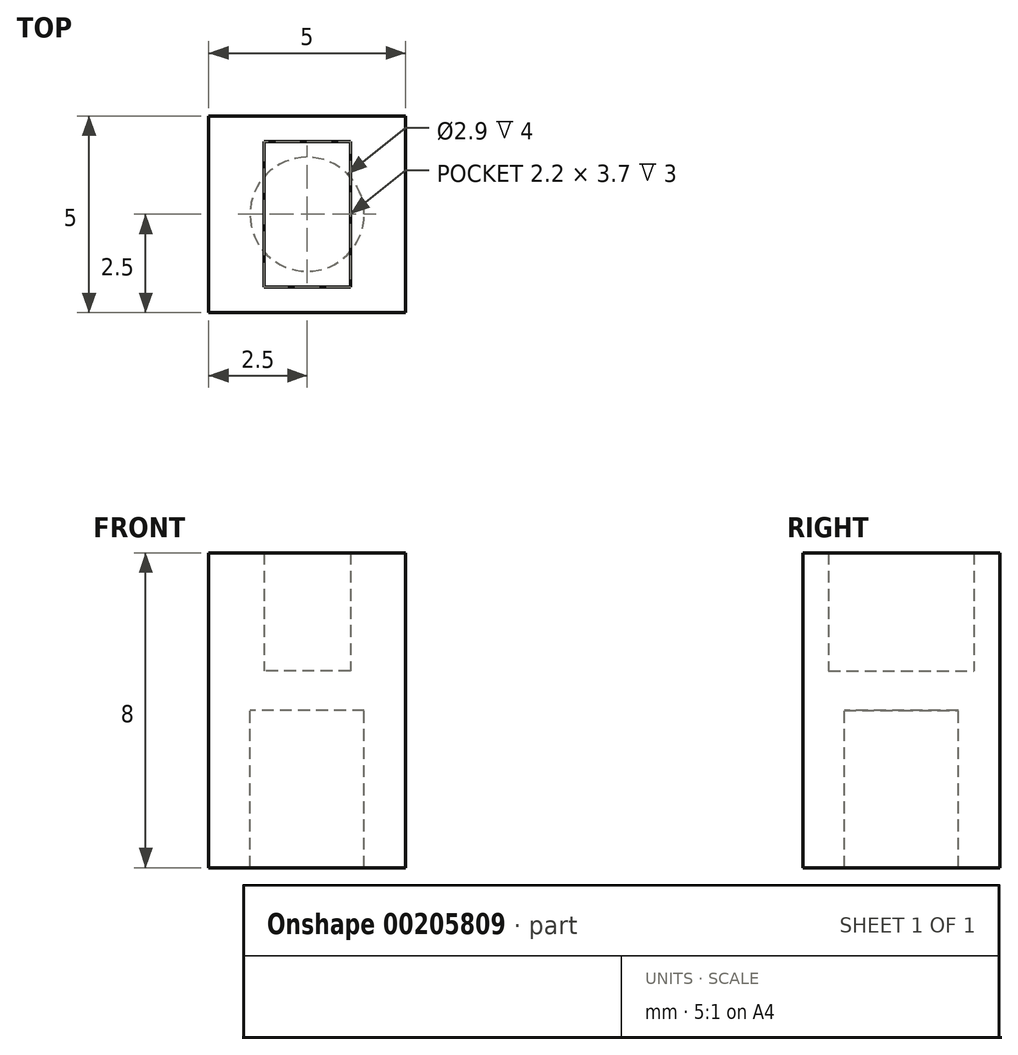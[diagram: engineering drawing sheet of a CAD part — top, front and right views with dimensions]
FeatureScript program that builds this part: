
annotation { "Feature Type Name" : "Feature", "Feature Type Description" : "" }
export const myFeature = defineFeature(function(context is Context, id is Id, definition is map)
    precondition{}
    {
        {
            var Q0;
            Q0=qCreatedBy(makeId("Top.planeOp"),FACE);
            var sketch = newSketch(context, id + "F0", { "sketchPlane" : qUnion([Q0])});
            skLineSegment(sketch, "E0.bottom", {"start": v(2.5, 2.5) * mm, "end": v(-2.5, 2.5) * mm});
            skLineSegment(sketch, "E0.top", {"start": v(2.5, -2.5) * mm, "end": v(-2.5, -2.5) * mm});
            skLineSegment(sketch, "E0.left", {"start": v(2.5, 2.5) * mm, "end": v(2.5, -2.5) * mm});
            skLineSegment(sketch, "E0.right", {"start": v(-2.5, 2.5) * mm, "end": v(-2.5, -2.5) * mm});
            skPoint(sketch, "E0.middle", {"position": v(0, 0) * mm});
            skSolve(sketch);
        }
        {
            var Q0;
            Q0=makeQuery(id+"F0.imprint","IMPRINT",FACE,{"disambiguationData":[TD([[makeQuery(id+"F0.imprint","IMPRINT",EDGE,{"derivedFrom":sQuery(id+"F0.wireOp",EDGE,"E0.bottom")}),1.0]])]});
            extrude(context, id + "F1", {"entities" : qUnion([Q0]), "depth" : 5 * mm});
        }
        {
            var Q0;
            Q0=makeQuery(id+"F1.opExtrude","CAP_FACE",FACE,{"disambiguationData":[OSD([sQuery(id+"F0.wireOp",EDGE,"E0.bottom"),sQuery(id+"F0.wireOp",EDGE,"E0.top"),sQuery(id+"F0.wireOp",EDGE,"E0.left"),sQuery(id+"F0.wireOp",EDGE,"E0.right")])],"isStart":false});
            var sketch = newSketch(context, id + "F2", { "sketchPlane" : qUnion([Q0])});
            skCircle(sketch, "E1", {"center": v(0, 0) * mm, "radius": 1.45 * mm});
            skSolve(sketch);
        }
        {
            var Q0;
            Q0=makeQuery(id+"F2.imprint","IMPRINT",FACE,{"disambiguationData":[TD([[makeQuery(id+"F2.imprint","IMPRINT",EDGE,{"derivedFrom":sQuery(id+"F2.wireOp",EDGE,"E1")}),1.0]])]});
            var Q1;
            Q1=sQuery(id+"F2.wireOp",EDGE,"E1");
            extrude(context, id + "F3", {"entities" : qUnion([Q0]), "operationType" : NewBodyOperationType.REMOVE, "surfaceEntities" : qUnion([Q1]), "endBound" : BoundingType.THROUGH_ALL, "oppositeDirection" : true, "depth" : 25 * mm});
        }
        {
            var Q0;
            Q0=makeQuery(id+"F1.opExtrude","CAP_FACE",FACE,{"disambiguationData":[OSD([sQuery(id+"F0.wireOp",EDGE,"E0.bottom"),sQuery(id+"F0.wireOp",EDGE,"E0.top"),sQuery(id+"F0.wireOp",EDGE,"E0.left"),sQuery(id+"F0.wireOp",EDGE,"E0.right")])],"isStart":false});
            var sketch = newSketch(context, id + "F4", { "sketchPlane" : qUnion([Q0])});
            skLineSegment(sketch, "E2.bottom", {"start": v(2.5, -2.5) * mm, "end": v(-2.5, -2.5) * mm});
            skLineSegment(sketch, "E2.top", {"start": v(2.5, 2.5) * mm, "end": v(-2.5, 2.5) * mm});
            skLineSegment(sketch, "E2.left", {"start": v(2.5, -2.5) * mm, "end": v(2.5, 2.5) * mm});
            skLineSegment(sketch, "E2.right", {"start": v(-2.5, -2.5) * mm, "end": v(-2.5, 2.5) * mm});
            skPoint(sketch, "E2.middle", {"position": v(0, 0) * mm});
            skLineSegment(sketch, "E3.bottom", {"start": v(1.1, -1.85) * mm, "end": v(-1.1, -1.85) * mm});
            skLineSegment(sketch, "E3.top", {"start": v(1.1, 1.85) * mm, "end": v(-1.1, 1.85) * mm});
            skLineSegment(sketch, "E3.left", {"start": v(1.1, -1.85) * mm, "end": v(1.1, 1.85) * mm});
            skLineSegment(sketch, "E3.right", {"start": v(-1.1, -1.85) * mm, "end": v(-1.1, 1.85) * mm});
            skSolve(sketch);
        }
        {
            var Q0;
            Q0=qSketchRegion(id+"F4",true);
            extrude(context, id + "F5", {"entities" : qUnion([Q0]), "operationType" : NewBodyOperationType.ADD, "depth" : 3 * mm});
        }
        {
            var Q0;
            Q0=makeQuery(id+"F4.imprint","IMPRINT",FACE,{"disambiguationData":[TD([[makeQuery(id+"F4.imprint","IMPRINT",EDGE,{"derivedFrom":sQuery(id+"F4.wireOp",EDGE,"E2.bottom")}),-1.0]])]});
            var Q1;
            {var subQ0=sQuery(id+"F4.wireOp",EDGE,"E3.top");Q1=makeQuery(id+"F4.imprint","IMPRINT",FACE,{"disambiguationData":[TD([[makeQuery(id+"F4.imprint","IMPRINT",EDGE,{"derivedFrom":subQ0}),1.0]])]});}
            var Q2;
            {var subQ0=sQuery(id+"F4.wireOp",EDGE,"E3.right");var subQ1=makeQuery(id+"F3.boolean.opBoolean","COPY",EDGE,{"derivedFrom":makeQuery(id+"F3.opExtrude","CAP_EDGE",EDGE,{"disambiguationData":[OSD([sQuery(id+"F2.wireOp",EDGE,"E1")])],"isStart":true})});var subQ2=makeQuery(id+"F4.imprint","INTERSECT",VERTEX,{"disambiguationData":[OD(0.0)],"derivedFrom":[subQ1,subQ0]});Q2=makeQuery(id+"F4.imprint","IMPRINT",FACE,{"disambiguationData":[TD([[makeQuery(id+"F4.imprint","IMPRINT",EDGE,{"disambiguationData":[TD([[subQ2,-1.0]])],"derivedFrom":subQ0}),1.0]])]});}
            var Q3;
            {var subQ0=sQuery(id+"F4.wireOp",EDGE,"E3.left");var subQ1=makeQuery(id+"F3.boolean.opBoolean","COPY",EDGE,{"derivedFrom":makeQuery(id+"F3.opExtrude","CAP_EDGE",EDGE,{"disambiguationData":[OSD([sQuery(id+"F2.wireOp",EDGE,"E1")])],"isStart":true})});var subQ2=makeQuery(id+"F4.imprint","INTERSECT",VERTEX,{"disambiguationData":[OD(0.0)],"derivedFrom":[subQ1,subQ0]});Q3=makeQuery(id+"F4.imprint","IMPRINT",FACE,{"disambiguationData":[TD([[makeQuery(id+"F4.imprint","IMPRINT",EDGE,{"disambiguationData":[TD([[subQ2,-1.0]])],"derivedFrom":subQ0}),1.0]])]});}
            var Q4;
            {var subQ0=sQuery(id+"F4.wireOp",EDGE,"E3.left");var subQ1=makeQuery(id+"F3.boolean.opBoolean","COPY",EDGE,{"derivedFrom":makeQuery(id+"F3.opExtrude","CAP_EDGE",EDGE,{"disambiguationData":[OSD([sQuery(id+"F2.wireOp",EDGE,"E1")])],"isStart":true})});var subQ2=makeQuery(id+"F4.imprint","INTERSECT",VERTEX,{"disambiguationData":[OD(0.0)],"derivedFrom":[subQ1,subQ0]});Q4=makeQuery(id+"F4.imprint","IMPRINT",FACE,{"disambiguationData":[TD([[makeQuery(id+"F4.imprint","IMPRINT",EDGE,{"disambiguationData":[TD([[subQ2,-1.0]])],"derivedFrom":subQ0}),-1.0]])]});}
            var Q5;
            {var subQ0=sQuery(id+"F4.wireOp",EDGE,"E3.bottom");Q5=makeQuery(id+"F4.imprint","IMPRINT",FACE,{"disambiguationData":[TD([[makeQuery(id+"F4.imprint","IMPRINT",EDGE,{"derivedFrom":subQ0}),-1.0]])]});}
            extrude(context, id + "F6", {"entities" : qUnion([Q0, Q1, Q2, Q3, Q4, Q5]), "operationType" : NewBodyOperationType.ADD, "oppositeDirection" : true, "depth" : 1 * mm});
        }
    });
